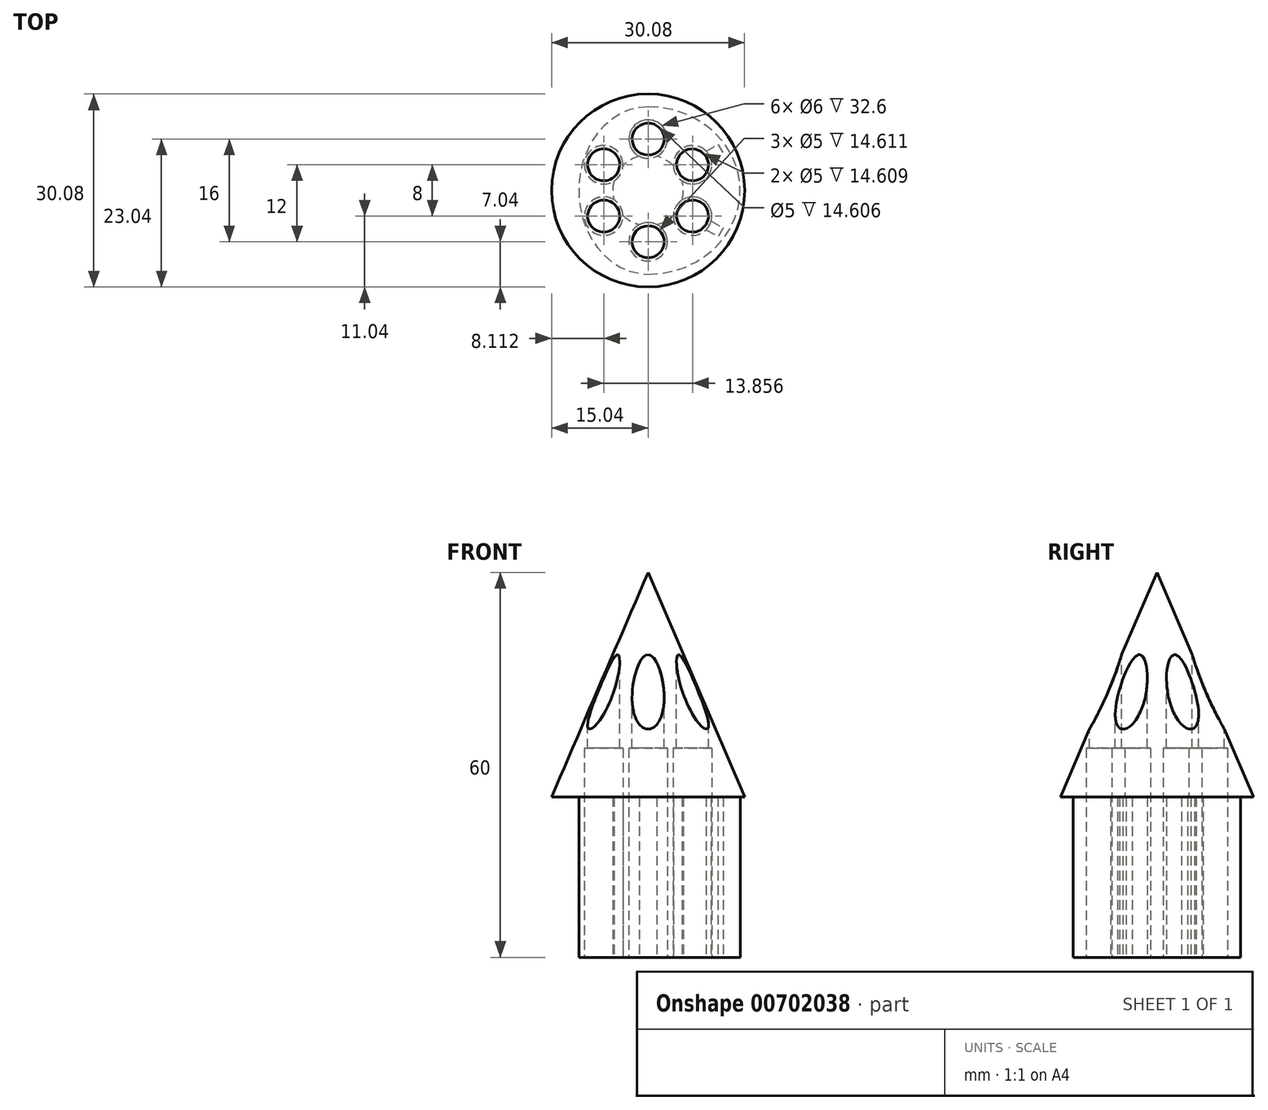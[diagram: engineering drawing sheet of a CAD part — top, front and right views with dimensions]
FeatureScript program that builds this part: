
annotation { "Feature Type Name" : "Feature", "Feature Type Description" : "" }
export const myFeature = defineFeature(function(context is Context, id is Id, definition is map)
    precondition{}
    {
        {
            var Q0;
            Q0=qCreatedBy(makeId("Top.planeOp"),FACE);
            var sketch = newSketch(context, id + "F0", { "sketchPlane" : qUnion([Q0])});
            skEllipticalArc(sketch, "E0", {});
            skEllipticalArc(sketch, "E1", {});
            skPoint(sketch, "E2", {"position": v(0, 13.04) * mm});
            skPoint(sketch, "E3", {"position": v(0, -13.04) * mm});
            const initialGuessF0  = {"E0": [0, 0, 0, 1, 0.013043729588389395, 0.010801234647977508, 0, 3.141592653589793], "E1": [0, 0, 0, 1, 0.013043729588389395, 0.014342294840615962, 3.141592653589793, 6.283185307179586]};
            skSetInitialGuess(sketch, initialGuessF0);
            skSolve(sketch);
        }
        {
            var Q0;
            Q0 = qSketchRegion(id + "F0", true);
            extrude(context, id + "F1", {"entities" : qUnion([Q0]), "depth" : 25 * mm, "offsetDistance" : 25 * mm});
        }
        {
            var Q0;
            Q0=qCreatedBy(makeId("Right.planeOp"),FACE);
            var sketch = newSketch(context, id + "F2", { "sketchPlane" : qUnion([Q0])});
            skLineSegment(sketch, "E4.0", {"start": v(13.04, 25) * mm, "end": v(-13.04, 25) * mm});
            skLineSegment(sketch, "E5", {"start": v(0, 25) * mm, "end": v(15.04, 25) * mm});
            skLineSegment(sketch, "E6", {"start": v(15.04, 25) * mm, "end": v(0, 60) * mm});
            skLineSegment(sketch, "E7", {"start": v(0, 60) * mm, "end": v(0, 25) * mm});
            skSolve(sketch);
        }
        {
            var Q0;
            Q0 = qSketchRegion(id + "F2", true);
            var Q1;
            Q1=sQuery(id+"F2.wireOp",EDGE,"E7");
            revolve(context, id + "F3", {"operationType" : NewBodyOperationType.ADD, "entities" : qUnion([Q0]), "axis" : qUnion([Q1]), "revolveType" : RevolveType.FULL});
        }
        {
            var Q0;
            Q0=qCreatedBy(makeId("Top.planeOp"),FACE);
            cPlane(context, id + "F4", {"entities" : qUnion([Q0]), "cplaneType" : CPlaneType.OFFSET, "offset" : 80 * mm, "width" : 150 * mm, "height" : 150 * mm});
        }
        {
            var Q0;
            Q0=qCreatedBy(id+"F4.planeOp",FACE);
            var sketch = newSketch(context, id + "F5", { "sketchPlane" : qUnion([Q0])});
            skCircle(sketch, "E8", {"center": v(0, 8) * mm, "radius": 2.5 * mm});
            skCircle(sketch, "E9.1.0", {"center": v(-6.93, 4) * mm, "radius": 2.5 * mm});
            skCircle(sketch, "E9.2.0", {"center": v(-6.93, -4) * mm, "radius": 2.5 * mm});
            skCircle(sketch, "E9.3.0", {"center": v(0, -8) * mm, "radius": 2.5 * mm});
            skCircle(sketch, "E9.4.0", {"center": v(6.93, -4) * mm, "radius": 2.5 * mm});
            skCircle(sketch, "E9.5.0", {"center": v(6.93, 4) * mm, "radius": 2.5 * mm});
            skPoint(sketch, "E9.center", {"position": v(0, 0) * mm});
            skSolve(sketch);
        }
        {
            var Q0;
            Q0=makeQuery(id+"F5.imprint","IMPRINT",FACE,{"disambiguationData":[TD([[makeQuery(id+"F5.imprint","IMPRINT",EDGE,{"derivedFrom":sQuery(id+"F5.wireOp",EDGE,"E8")}),1.0]])]});
            var Q1;
            Q1=makeQuery(id+"F5.imprint","IMPRINT",FACE,{"disambiguationData":[TD([[makeQuery(id+"F5.imprint","IMPRINT",EDGE,{"derivedFrom":sQuery(id+"F5.wireOp",EDGE,"E9.5.0")}),1.0]])]});
            var Q2;
            Q2=makeQuery(id+"F5.imprint","IMPRINT",FACE,{"disambiguationData":[TD([[makeQuery(id+"F5.imprint","IMPRINT",EDGE,{"derivedFrom":sQuery(id+"F5.wireOp",EDGE,"E9.4.0")}),1.0]])]});
            var Q3;
            Q3=makeQuery(id+"F5.imprint","IMPRINT",FACE,{"disambiguationData":[TD([[makeQuery(id+"F5.imprint","IMPRINT",EDGE,{"derivedFrom":sQuery(id+"F5.wireOp",EDGE,"E9.3.0")}),1.0]])]});
            var Q4;
            Q4=makeQuery(id+"F5.imprint","IMPRINT",FACE,{"disambiguationData":[TD([[makeQuery(id+"F5.imprint","IMPRINT",EDGE,{"derivedFrom":sQuery(id+"F5.wireOp",EDGE,"E9.2.0")}),1.0]])]});
            var Q5;
            Q5=makeQuery(id+"F5.imprint","IMPRINT",FACE,{"disambiguationData":[TD([[makeQuery(id+"F5.imprint","IMPRINT",EDGE,{"derivedFrom":sQuery(id+"F5.wireOp",EDGE,"E9.1.0")}),1.0]])]});
            extrude(context, id + "F6", {"entities" : qUnion([Q0, Q1, Q2, Q3, Q4, Q5]), "operationType" : NewBodyOperationType.REMOVE, "oppositeDirection" : true, "depth" : 80 * mm, "offsetDistance" : 25 * mm});
        }
        {
            var Q0;
            Q0=makeQuery(id+"F1.opExtrude","CAP_FACE",FACE,{"disambiguationData":[OSD([sQuery(id+"F0.wireOp",EDGE,"E0"),sQuery(id+"F0.wireOp",EDGE,"E1")])],"isStart":true});
            var sketch = newSketch(context, id + "F7", { "sketchPlane" : qUnion([Q0])});
            skCircle(sketch, "E10", {"center": v(0, 0) * mm, "radius": 5.5 * mm});
            skSolve(sketch);
        }
        {
            var Q0;
            Q0 = qSketchRegion(id + "F7", true);
            extrude(context, id + "F8", {"entities" : qUnion([Q0]), "operationType" : NewBodyOperationType.REMOVE, "oppositeDirection" : true, "depth" : 25 * mm, "offsetDistance" : 25 * mm});
        }
        {
            var Q0;
            Q0=makeQuery(id+"F1.opExtrude","CAP_FACE",FACE,{"disambiguationData":[OSD([sQuery(id+"F0.wireOp",EDGE,"E0"),sQuery(id+"F0.wireOp",EDGE,"E1")])],"isStart":true});
            var sketch = newSketch(context, id + "F9", { "sketchPlane" : qUnion([Q0])});
            skLineSegment(sketch, "E11.bottom", {"start": v(0.78, 0) * mm, "end": v(-0.78, 0) * mm});
            skLineSegment(sketch, "E11.top", {"start": v(0.78, 13.04) * mm, "end": v(-0.78, 13.04) * mm});
            skLineSegment(sketch, "E11.left", {"start": v(0.78, 0) * mm, "end": v(0.78, 13.04) * mm});
            skLineSegment(sketch, "E11.right", {"start": v(-0.78, 0) * mm, "end": v(-0.78, 13.04) * mm});
            skPoint(sketch, "E11.middle", {"position": v(0, 6.52) * mm});
            skLineSegment(sketch, "E12.1.0", {"start": v(-0.4, -0.68) * mm, "end": v(-11.69, 5.85) * mm});
            skLineSegment(sketch, "E12.1.1", {"start": v(-10.9, 7.2) * mm, "end": v(-11.69, 5.85) * mm});
            skLineSegment(sketch, "E12.1.2", {"start": v(0.4, 0.68) * mm, "end": v(-10.9, 7.2) * mm});
            skLineSegment(sketch, "E12.1.3", {"start": v(0.4, 0.68) * mm, "end": v(-0.4, -0.68) * mm});
            skLineSegment(sketch, "E12.2.0", {"start": v(0.4, -0.68) * mm, "end": v(-10.9, -7.2) * mm});
            skLineSegment(sketch, "E12.2.1", {"start": v(-11.69, -5.85) * mm, "end": v(-10.9, -7.2) * mm});
            skLineSegment(sketch, "E12.2.2", {"start": v(-0.4, 0.68) * mm, "end": v(-11.69, -5.85) * mm});
            skLineSegment(sketch, "E12.2.3", {"start": v(-0.4, 0.68) * mm, "end": v(0.4, -0.68) * mm});
            skLineSegment(sketch, "E12.3.0", {"start": v(0.78, 0) * mm, "end": v(0.78, -13.04) * mm});
            skLineSegment(sketch, "E12.3.1", {"start": v(-0.78, -13.04) * mm, "end": v(0.78, -13.04) * mm});
            skLineSegment(sketch, "E12.3.2", {"start": v(-0.78, 0) * mm, "end": v(-0.78, -13.04) * mm});
            skLineSegment(sketch, "E12.3.3", {"start": v(-0.78, 0) * mm, "end": v(0.78, 0) * mm});
            skLineSegment(sketch, "E12.4.0", {"start": v(0.4, 0.68) * mm, "end": v(11.69, -5.85) * mm});
            skLineSegment(sketch, "E12.4.1", {"start": v(10.9, -7.2) * mm, "end": v(11.69, -5.85) * mm});
            skLineSegment(sketch, "E12.4.2", {"start": v(-0.4, -0.68) * mm, "end": v(10.9, -7.2) * mm});
            skLineSegment(sketch, "E12.4.3", {"start": v(-0.4, -0.68) * mm, "end": v(0.4, 0.68) * mm});
            skLineSegment(sketch, "E12.5.0", {"start": v(-0.4, 0.68) * mm, "end": v(10.9, 7.2) * mm});
            skLineSegment(sketch, "E12.5.1", {"start": v(11.69, 5.85) * mm, "end": v(10.9, 7.2) * mm});
            skLineSegment(sketch, "E12.5.2", {"start": v(0.4, -0.68) * mm, "end": v(11.69, 5.85) * mm});
            skLineSegment(sketch, "E12.5.3", {"start": v(0.4, -0.68) * mm, "end": v(-0.4, 0.68) * mm});
            skPoint(sketch, "E12.center", {"position": v(0, 0) * mm});
            skSolve(sketch);
        }
        {
            var Q0;
            {var subQ0=sQuery(id+"F9.wireOp",EDGE,"E12.1.1");Q0=makeQuery(id+"F9.imprint","IMPRINT",FACE,{"disambiguationData":[TD([[makeQuery(id+"F9.imprint","IMPRINT",EDGE,{"derivedFrom":subQ0}),1.0]])]});}
            var Q1;
            {var subQ0=sQuery(id+"F9.wireOp",EDGE,"E12.1.0");var subQ1=makeQuery(id+"F6.boolean.opBoolean","COPY",EDGE,{"derivedFrom":makeQuery(id+"F6.opExtrude","CAP_EDGE",EDGE,{"disambiguationData":[OSD([sQuery(id+"F5.wireOp",EDGE,"E9.2.0")])],"isStart":false})});var subQ2=makeQuery(id+"F9.imprint","INTERSECT",VERTEX,{"derivedFrom":[subQ1,subQ0]});Q1=makeQuery(id+"F9.imprint","IMPRINT",FACE,{"disambiguationData":[TD([[makeQuery(id+"F9.imprint","IMPRINT",EDGE,{"disambiguationData":[TD([[subQ2,1.0]])],"derivedFrom":subQ0}),-1.0]])]});}
            var Q2;
            {var subQ0=sQuery(id+"F9.wireOp",EDGE,"E12.2.2");var subQ1=sQuery(id+"F9.wireOp",EDGE,"E11.right");var subQ2=makeQuery(id+"F9.imprint","INTERSECT",VERTEX,{"derivedFrom":[subQ1,subQ0]});Q2=makeQuery(id+"F9.imprint","IMPRINT",FACE,{"disambiguationData":[TD([[makeQuery(id+"F9.imprint","IMPRINT",EDGE,{"disambiguationData":[TD([[subQ2,-1.0]])],"derivedFrom":subQ1}),1.0]])]});}
            var Q3;
            {var subQ0=sQuery(id+"F9.wireOp",EDGE,"E11.top");Q3=makeQuery(id+"F9.imprint","IMPRINT",FACE,{"disambiguationData":[TD([[makeQuery(id+"F9.imprint","IMPRINT",EDGE,{"derivedFrom":subQ0}),1.0]])]});}
            var Q4;
            {var subQ0=sQuery(id+"F9.wireOp",EDGE,"E11.left");var subQ1=makeQuery(id+"F6.boolean.opBoolean","COPY",EDGE,{"derivedFrom":makeQuery(id+"F6.opExtrude","CAP_EDGE",EDGE,{"disambiguationData":[OSD([sQuery(id+"F5.wireOp",EDGE,"E9.3.0")])],"isStart":false})});var subQ2=makeQuery(id+"F9.imprint","INTERSECT",VERTEX,{"derivedFrom":[subQ1,subQ0]});Q4=makeQuery(id+"F9.imprint","IMPRINT",FACE,{"disambiguationData":[TD([[makeQuery(id+"F9.imprint","IMPRINT",EDGE,{"disambiguationData":[TD([[subQ2,1.0]])],"derivedFrom":subQ0}),1.0]])]});}
            var Q5;
            {var subQ0=sQuery(id+"F9.wireOp",EDGE,"E12.5.0");var subQ1=sQuery(id+"F9.wireOp",EDGE,"E11.left");var subQ2=makeQuery(id+"F9.imprint","INTERSECT",VERTEX,{"derivedFrom":[subQ1,subQ0]});Q5=makeQuery(id+"F9.imprint","IMPRINT",FACE,{"disambiguationData":[TD([[makeQuery(id+"F9.imprint","IMPRINT",EDGE,{"disambiguationData":[TD([[subQ2,-1.0]])],"derivedFrom":subQ1}),1.0]])]});}
            var Q6;
            {var subQ1=sQuery(id+"F9.wireOp",EDGE,"E11.left");var subQ6=sQuery(id+"F9.wireOp",EDGE,"E12.4.0");var subQ9=makeQuery(id+"F9.imprint","INTERSECT",VERTEX,{"derivedFrom":[subQ1,subQ6]});Q6=makeQuery(id+"F9.imprint","IMPRINT",FACE,{"disambiguationData":[TD([[makeQuery(id+"F9.imprint","IMPRINT",EDGE,{"disambiguationData":[TD([[subQ9,-1.0]])],"derivedFrom":subQ1}),-1.0]])]});}
            var Q7;
            {var subQ0=sQuery(id+"F9.wireOp",EDGE,"E12.5.0");var subQ1=makeQuery(id+"F6.boolean.opBoolean","COPY",EDGE,{"derivedFrom":makeQuery(id+"F6.opExtrude","CAP_EDGE",EDGE,{"disambiguationData":[OSD([sQuery(id+"F5.wireOp",EDGE,"E9.4.0")])],"isStart":false})});var subQ2=makeQuery(id+"F9.imprint","INTERSECT",VERTEX,{"derivedFrom":[subQ1,subQ0]});Q7=makeQuery(id+"F9.imprint","IMPRINT",FACE,{"disambiguationData":[TD([[makeQuery(id+"F9.imprint","IMPRINT",EDGE,{"disambiguationData":[TD([[subQ2,1.0]])],"derivedFrom":subQ0}),-1.0]])]});}
            var Q8;
            {var subQ0=sQuery(id+"F9.wireOp",EDGE,"E12.5.1");Q8=makeQuery(id+"F9.imprint","IMPRINT",FACE,{"disambiguationData":[TD([[makeQuery(id+"F9.imprint","IMPRINT",EDGE,{"derivedFrom":subQ0}),1.0]])]});}
            var Q9;
            {var subQ0=sQuery(id+"F9.wireOp",EDGE,"E12.4.1");Q9=makeQuery(id+"F9.imprint","IMPRINT",FACE,{"disambiguationData":[TD([[makeQuery(id+"F9.imprint","IMPRINT",EDGE,{"derivedFrom":subQ0}),1.0]])]});}
            var Q10;
            {var subQ0=sQuery(id+"F9.wireOp",EDGE,"E12.4.0");var subQ1=makeQuery(id+"F6.boolean.opBoolean","COPY",EDGE,{"derivedFrom":makeQuery(id+"F6.opExtrude","CAP_EDGE",EDGE,{"disambiguationData":[OSD([sQuery(id+"F5.wireOp",EDGE,"E9.5.0")])],"isStart":false})});var subQ2=makeQuery(id+"F9.imprint","INTERSECT",VERTEX,{"derivedFrom":[subQ1,subQ0]});Q10=makeQuery(id+"F9.imprint","IMPRINT",FACE,{"disambiguationData":[TD([[makeQuery(id+"F9.imprint","IMPRINT",EDGE,{"disambiguationData":[TD([[subQ2,1.0]])],"derivedFrom":subQ0}),-1.0]])]});}
            var Q11;
            {var subQ0=sQuery(id+"F9.wireOp",EDGE,"E12.5.2");var subQ1=sQuery(id+"F9.wireOp",EDGE,"E12.3.0");var subQ2=makeQuery(id+"F9.imprint","INTERSECT",VERTEX,{"derivedFrom":[subQ1,subQ0]});Q11=makeQuery(id+"F9.imprint","IMPRINT",FACE,{"disambiguationData":[TD([[makeQuery(id+"F9.imprint","IMPRINT",EDGE,{"disambiguationData":[TD([[subQ2,-1.0]])],"derivedFrom":subQ1}),1.0]])]});}
            var Q12;
            {var subQ1=sQuery(id+"F9.wireOp",EDGE,"E12.2.0");var subQ5=sQuery(id+"F9.wireOp",EDGE,"E12.4.2");var subQ9=makeQuery(id+"F9.imprint","INTERSECT",VERTEX,{"derivedFrom":[subQ1,subQ5]});Q12=makeQuery(id+"F9.imprint","IMPRINT",FACE,{"disambiguationData":[TD([[makeQuery(id+"F9.imprint","IMPRINT",EDGE,{"disambiguationData":[TD([[subQ9,-1.0]])],"derivedFrom":subQ1}),1.0]])]});}
            var Q13;
            {var subQ0=sQuery(id+"F9.wireOp",EDGE,"E12.3.0");var subQ1=makeQuery(id+"F6.boolean.opBoolean","COPY",EDGE,{"derivedFrom":makeQuery(id+"F6.opExtrude","CAP_EDGE",EDGE,{"disambiguationData":[OSD([sQuery(id+"F5.wireOp",EDGE,"E8")])],"isStart":false})});var subQ2=makeQuery(id+"F9.imprint","INTERSECT",VERTEX,{"derivedFrom":[subQ1,subQ0]});Q13=makeQuery(id+"F9.imprint","IMPRINT",FACE,{"disambiguationData":[TD([[makeQuery(id+"F9.imprint","IMPRINT",EDGE,{"disambiguationData":[TD([[subQ2,1.0]])],"derivedFrom":subQ0}),-1.0]])]});}
            var Q14;
            {var subQ0=sQuery(id+"F9.wireOp",EDGE,"E12.3.1");Q14=makeQuery(id+"F9.imprint","IMPRINT",FACE,{"disambiguationData":[TD([[makeQuery(id+"F9.imprint","IMPRINT",EDGE,{"derivedFrom":subQ0}),1.0]])]});}
            var Q15;
            {var subQ0=sQuery(id+"F9.wireOp",EDGE,"E12.2.1");Q15=makeQuery(id+"F9.imprint","IMPRINT",FACE,{"disambiguationData":[TD([[makeQuery(id+"F9.imprint","IMPRINT",EDGE,{"derivedFrom":subQ0}),1.0]])]});}
            var Q16;
            {var subQ0=sQuery(id+"F9.wireOp",EDGE,"E12.2.0");var subQ1=makeQuery(id+"F6.boolean.opBoolean","COPY",EDGE,{"derivedFrom":makeQuery(id+"F6.opExtrude","CAP_EDGE",EDGE,{"disambiguationData":[OSD([sQuery(id+"F5.wireOp",EDGE,"E9.1.0")])],"isStart":false})});var subQ2=makeQuery(id+"F9.imprint","INTERSECT",VERTEX,{"derivedFrom":[subQ1,subQ0]});Q16=makeQuery(id+"F9.imprint","IMPRINT",FACE,{"disambiguationData":[TD([[makeQuery(id+"F9.imprint","IMPRINT",EDGE,{"disambiguationData":[TD([[subQ2,1.0]])],"derivedFrom":subQ0}),-1.0]])]});}
            var Q17;
            {var subQ0=sQuery(id+"F9.wireOp",EDGE,"E12.3.2");var subQ1=sQuery(id+"F9.wireOp",EDGE,"E12.1.0");var subQ2=makeQuery(id+"F9.imprint","INTERSECT",VERTEX,{"derivedFrom":[subQ1,subQ0]});Q17=makeQuery(id+"F9.imprint","IMPRINT",FACE,{"disambiguationData":[TD([[makeQuery(id+"F9.imprint","IMPRINT",EDGE,{"disambiguationData":[TD([[subQ2,-1.0]])],"derivedFrom":subQ1}),1.0]])]});}
            var Q18;
            {var subQ0=sQuery(id+"F9.wireOp",EDGE,"E12.2.2");var subQ1=sQuery(id+"F9.wireOp",EDGE,"E11.right");var subQ2=makeQuery(id+"F9.imprint","INTERSECT",VERTEX,{"derivedFrom":[subQ1,subQ0]});Q18=makeQuery(id+"F9.imprint","IMPRINT",FACE,{"disambiguationData":[TD([[makeQuery(id+"F9.imprint","IMPRINT",EDGE,{"disambiguationData":[TD([[subQ2,-1.0]])],"derivedFrom":subQ1}),-1.0]])]});}
            var Q19;
            {var subQ0=sQuery(id+"F9.wireOp",EDGE,"E12.4.0");var subQ1=sQuery(id+"F9.wireOp",EDGE,"E11.left");var subQ2=makeQuery(id+"F9.imprint","INTERSECT",VERTEX,{"derivedFrom":[subQ1,subQ0]});Q19=makeQuery(id+"F9.imprint","IMPRINT",FACE,{"disambiguationData":[TD([[makeQuery(id+"F9.imprint","IMPRINT",EDGE,{"disambiguationData":[TD([[subQ2,-1.0]])],"derivedFrom":subQ1}),1.0]])]});}
            var Q20;
            {var subQ1=sQuery(id+"F9.wireOp",EDGE,"E11.left");var subQ3=sQuery(id+"F9.wireOp",EDGE,"E12.4.0");var subQ4=makeQuery(id+"F9.imprint","INTERSECT",VERTEX,{"derivedFrom":[subQ1,subQ3]});Q20=makeQuery(id+"F9.imprint","IMPRINT",FACE,{"disambiguationData":[TD([[makeQuery(id+"F9.imprint","IMPRINT",EDGE,{"disambiguationData":[TD([[subQ4,-1.0]])],"derivedFrom":subQ3}),-1.0]])]});}
            var Q21;
            {var subQ0=sQuery(id+"F9.wireOp",EDGE,"E12.5.2");var subQ5=sQuery(id+"F9.wireOp",EDGE,"E12.3.0");var subQ6=makeQuery(id+"F9.imprint","INTERSECT",VERTEX,{"derivedFrom":[subQ5,subQ0]});Q21=makeQuery(id+"F9.imprint","IMPRINT",FACE,{"disambiguationData":[TD([[makeQuery(id+"F9.imprint","IMPRINT",EDGE,{"disambiguationData":[TD([[subQ6,-1.0]])],"derivedFrom":subQ5}),-1.0]])]});}
            var Q22;
            {var subQ0=sQuery(id+"F9.wireOp",EDGE,"E12.4.2");var subQ5=sQuery(id+"F9.wireOp",EDGE,"E12.2.0");var subQ6=makeQuery(id+"F9.imprint","INTERSECT",VERTEX,{"derivedFrom":[subQ5,subQ0]});Q22=makeQuery(id+"F9.imprint","IMPRINT",FACE,{"disambiguationData":[TD([[makeQuery(id+"F9.imprint","IMPRINT",EDGE,{"disambiguationData":[TD([[subQ6,-1.0]])],"derivedFrom":subQ5}),-1.0]])]});}
            var Q23;
            {var subQ0=sQuery(id+"F9.wireOp",EDGE,"E12.3.2");var subQ5=sQuery(id+"F9.wireOp",EDGE,"E12.1.0");var subQ6=makeQuery(id+"F9.imprint","INTERSECT",VERTEX,{"derivedFrom":[subQ5,subQ0]});Q23=makeQuery(id+"F9.imprint","IMPRINT",FACE,{"disambiguationData":[TD([[makeQuery(id+"F9.imprint","IMPRINT",EDGE,{"disambiguationData":[TD([[subQ6,-1.0]])],"derivedFrom":subQ5}),-1.0]])]});}
            extrude(context, id + "F10", {"entities" : qUnion([Q0, Q1, Q2, Q3, Q4, Q5, Q6, Q7, Q8, Q9, Q10, Q11, Q12, Q13, Q14, Q15, Q16, Q17, Q18, Q19, Q20, Q21, Q22, Q23]), "operationType" : NewBodyOperationType.REMOVE, "oppositeDirection" : true, "depth" : 25 * mm, "offsetDistance" : 25 * mm});
        }
        {
            var Q0;
            Q0=qCreatedBy(makeId("Top.planeOp"),FACE);
            var sketch = newSketch(context, id + "F11", { "sketchPlane" : qUnion([Q0])});
            skCircle(sketch, "E13", {"center": v(0, -8) * mm, "radius": 3 * mm});
            skCircle(sketch, "E14.1.0", {"center": v(6.93, -4) * mm, "radius": 3 * mm});
            skCircle(sketch, "E14.2.0", {"center": v(6.93, 4) * mm, "radius": 3 * mm});
            skCircle(sketch, "E14.3.0", {"center": v(0, 8) * mm, "radius": 3 * mm});
            skCircle(sketch, "E14.4.0", {"center": v(-6.93, 4) * mm, "radius": 3 * mm});
            skCircle(sketch, "E14.5.0", {"center": v(-6.93, -4) * mm, "radius": 3 * mm});
            skPoint(sketch, "E14.center", {"position": v(0, 0) * mm});
            skSolve(sketch);
        }
        {
            var Q0;
            Q0=makeQuery(id+"F11.imprint","IMPRINT",FACE,{"disambiguationData":[TD([[makeQuery(id+"F11.imprint","IMPRINT",EDGE,{"derivedFrom":sQuery(id+"F11.wireOp",EDGE,"E14.5.0")}),1.0]])]});
            var Q1;
            Q1=makeQuery(id+"F11.imprint","IMPRINT",FACE,{"disambiguationData":[TD([[makeQuery(id+"F11.imprint","IMPRINT",EDGE,{"derivedFrom":sQuery(id+"F11.wireOp",EDGE,"E13")}),1.0]])]});
            var Q2;
            Q2=makeQuery(id+"F11.imprint","IMPRINT",FACE,{"disambiguationData":[TD([[makeQuery(id+"F11.imprint","IMPRINT",EDGE,{"derivedFrom":sQuery(id+"F11.wireOp",EDGE,"E14.1.0")}),1.0]])]});
            var Q3;
            Q3=makeQuery(id+"F11.imprint","IMPRINT",FACE,{"disambiguationData":[TD([[makeQuery(id+"F11.imprint","IMPRINT",EDGE,{"derivedFrom":sQuery(id+"F11.wireOp",EDGE,"E14.2.0")}),1.0]])]});
            var Q4;
            Q4=makeQuery(id+"F11.imprint","IMPRINT",FACE,{"disambiguationData":[TD([[makeQuery(id+"F11.imprint","IMPRINT",EDGE,{"derivedFrom":sQuery(id+"F11.wireOp",EDGE,"E14.3.0")}),1.0]])]});
            var Q5;
            Q5=makeQuery(id+"F11.imprint","IMPRINT",FACE,{"disambiguationData":[TD([[makeQuery(id+"F11.imprint","IMPRINT",EDGE,{"derivedFrom":sQuery(id+"F11.wireOp",EDGE,"E14.4.0")}),1.0]])]});
            extrude(context, id + "F12", {"entities" : qUnion([Q0, Q1, Q2, Q3, Q4, Q5]), "operationType" : NewBodyOperationType.REMOVE, "depth" : 32.6 * mm, "offsetDistance" : 25 * mm});
        }
    });
